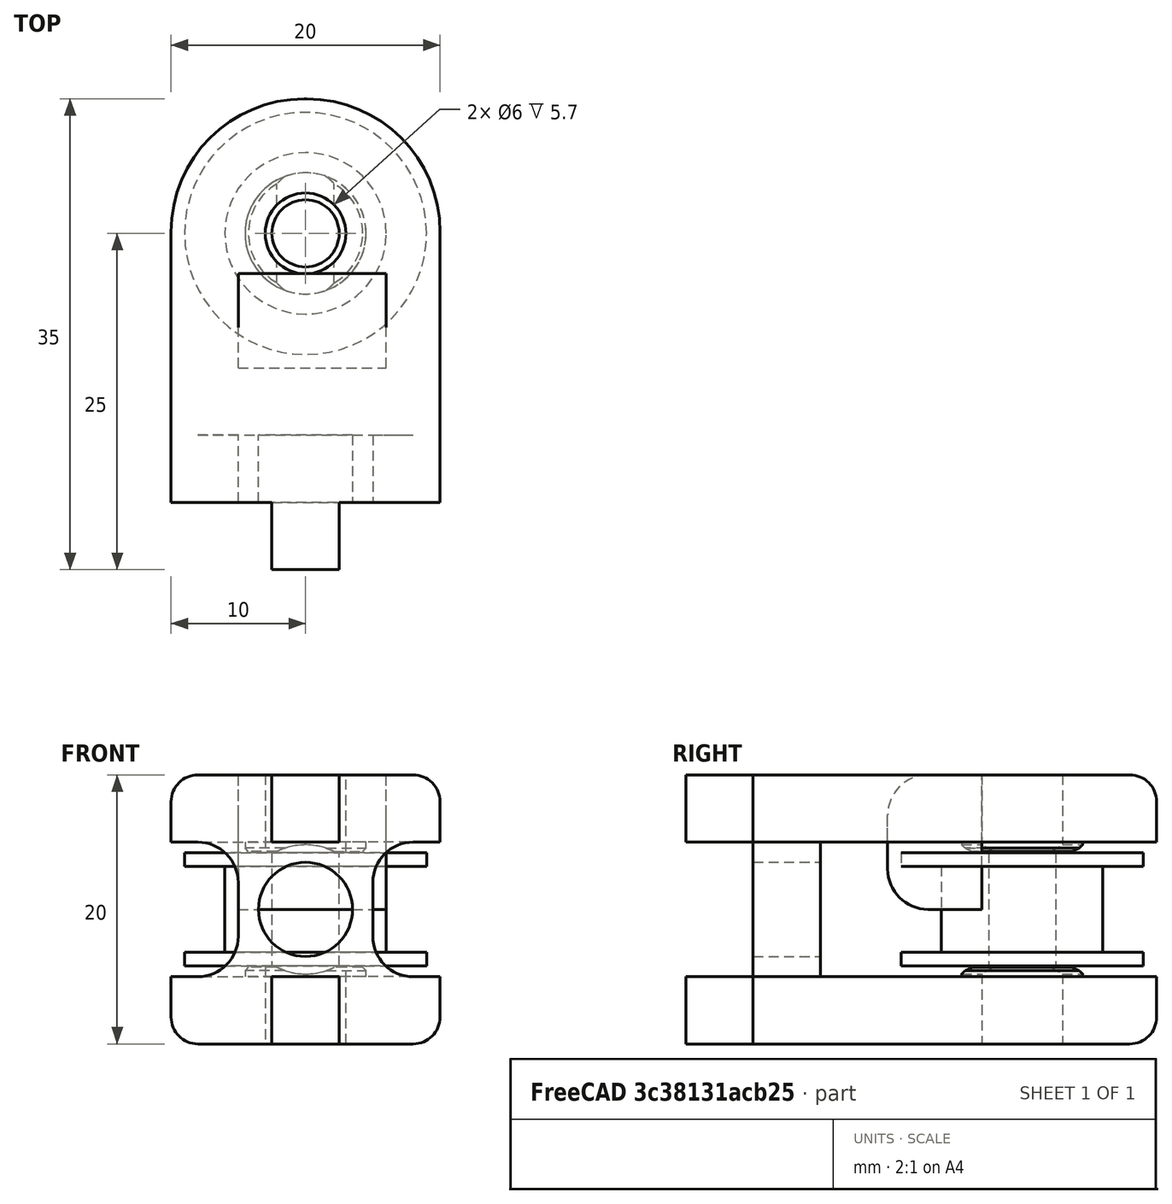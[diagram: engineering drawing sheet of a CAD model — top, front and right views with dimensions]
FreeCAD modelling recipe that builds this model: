
FCSTD DOCUMENT  (FreeCAD 0.20R29177 (Git))
Label: PoleaAcabados1
License: All rights reserved
LicenseURL: http://en.wikipedia.org/wiki/All_rights_reserved
objects: Part::Cylinder×7, Part::Cut×5, Part::Box×4, Part::FeaturePython×3, Part::MultiFuse×3, Part::Chamfer×3, Part::Refine×2, Part::Fillet×2, Part::Fuse×1, Spreadsheet::Sheet×1, PartDesign::FeatureBase×1, PartDesign::Fillet×1, PartDesign::Body×1
note: 33 computed .brp shape members not serialized (recipe doc carries the construction recipe); baked Part::Feature solids carry a one-line shape summary decoded from their .brp

FEATURE [Part::Cylinder] Cylinder002  label="Cilindro002"
  Angle = 360
  AttacherType = Attacher::AttachEngine3D
  FirstAngle = 0
  Height = 1
  Placement = pos=(0,0,-4.2) rot=(0,0,1;0rad)
  Radius = 9
  SecondAngle = 0
FEATURE [Part::Cylinder] Cylinder003  label="Cilindro003"
  Angle = 360
  AttacherType = Attacher::AttachEngine3D
  FirstAngle = 0
  Height = 10
  Placement = pos=(0,0,-5) rot=(0,0,1;0rad)
  Radius = 2.5
  SecondAngle = 0
FEATURE [Part::Fuse] Fusion001
  Base = -> Cylinder002
FEATURE [Part::Cut] Cut  label="Pulley"
  Base = -> Fusion001
  Placement = pos=(0,15,0) rot=(0,0,1;0rad)
  Tool = -> Cylinder003
  expr: .Placement.Base.y = Spreadsheet.viajPolea
FEATURE [Spreadsheet::Sheet] Spreadsheet
  cells = A1=Nombre; B1=Valor; A2=viajPolea; B2(viajPolea)=15; A3=tol; B3(tol)=1; A4=esp; B4(esp)=5; A5=prof; B5(prof)=20; A6=profMedio; B6(profMedio)==B5 / 2; A7=espDob; B7(espDob)==B4 * 2; A8=espMedio; B8(espMedio)==B4 / 2; A9=profMedREsp; B9(profMedREsp)==B6 - B4; A10=lonPol; B10(lonPol)==B2 + B6
FEATURE [Part::Box] Box  label="Base"
  AttacherType = Attacher::AttachEngine3D
  Height = 20
  Length = 20
  Placement = pos=(-10,-5,-10) rot=(0,0,1;0rad)
  Width = 5
  expr: .Placement.Base.x = -Spreadsheet.profMedio
  expr: .Placement.Base.y = -Spreadsheet.esp
  expr: .Placement.Base.z = -Spreadsheet.profMedio
  expr: Height = Spreadsheet.prof
  expr: Length = Spreadsheet.prof
  expr: Width = Spreadsheet.esp
FEATURE [Part::Box] Box001  label="pin0"
  AttacherType = Attacher::AttachEngine3D
  Height = 5
  Length = 5
  Placement = pos=(-2.5,-10,5) rot=(0,0,1;0rad)
  Width = 10
  expr: .Placement.Base.x = -Spreadsheet.espMedio
  expr: .Placement.Base.y = -Spreadsheet.espDob
  expr: .Placement.Base.z = Spreadsheet.profMedREsp
  expr: Height = Spreadsheet.esp
  expr: Length = Spreadsheet.esp
  expr: Width = Spreadsheet.espDob
FEATURE [Part::FeaturePython] Clone  label="pin001"  # Draft clone (typed FeaturePython)
  AttacherType = Attacher::AttachEngine3D
  Fuse = false
  Objects = -> [Box001]
  Placement = pos=(-2.5,-10,-10) rot=(0,0,1;0rad)
  Scale = (1,1,1)
  expr: .Placement.Base.y = -Spreadsheet.espDob
  expr: .Placement.Base.z = -Spreadsheet.profMedio
FEATURE [Part::Box] Box002  label="pared1"
  AttacherType = Attacher::AttachEngine3D
  Height = 5
  Length = 20
  Placement = pos=(-10,0,5) rot=(0,0,1;0rad)
  Width = 25
  expr: .Placement.Base.x = -Spreadsheet.profMedio
  expr: .Placement.Base.z = Spreadsheet.profMedREsp
  expr: Height = Spreadsheet.esp
  expr: Length = Spreadsheet.prof
  expr: Width = Spreadsheet.lonPol
FEATURE [Part::FeaturePython] Clone001  label="pared002"  # Draft clone (typed FeaturePython)
  AttacherType = Attacher::AttachEngine3D
  Fuse = false
  Objects = -> [Box002]
  Placement = pos=(-10,0,-10) rot=(0,0,1;0rad)
  Scale = (1,1,1)
  expr: .Placement.Base.z = -Spreadsheet.profMedio
FEATURE [Part::MultiFuse] Fusion
  Shapes = -> [Box,Box001,Clone,Box002,Clone001]
FEATURE [Part::Refine] Fusion002
  Source = -> Fusion
FEATURE [Part::Cylinder] Cylinder004  label="Cilindro004"
  Angle = 360
  AttacherType = Attacher::AttachEngine3D
  FirstAngle = 0
  Height = 30
  Placement = pos=(0,15,-15) rot=(0,0,1;0rad)
  Radius = 3
  SecondAngle = 0
  expr: .Placement.Base.y = Spreadsheet.viajPolea
FEATURE [Part::Box] Box007  label="Cubo005"
  AttacherType = Attacher::AttachEngine3D
  Height = 10
  Length = 11
  Placement = pos=(10,5,-5) rot=(0,0,1;0rad)
  Width = 7
FEATURE [PartDesign::FeatureBase] BaseFeature
  BaseFeature = -> Box007
FEATURE [PartDesign::Fillet] Fillet
  Base = -> BaseFeature [Edge10,Edge9]
  BaseFeature = -> BaseFeature
  Radius = 3
  SupportTransform = false
  UseAllEdges = false
FEATURE [PartDesign::Body] Body
  BaseFeature = -> Box007
  Group = -> [BaseFeature,Fillet]
  Origin = -> Origin
  Placement = pos=(-5,5,0) rot=(0,0,1;0rad)
  Tip = -> Fillet
FEATURE [Part::FeaturePython] Array  # Draft array (typed FeaturePython)
  AlwaysSyncPlacement = false
  Angle = 180
  ArrayType = 1
  Axis = (0,0,1)
  Base = -> Body
  Center = (0,0,0)
  Count = 2
  ExpandArray = false
  Fuse = false
  IntervalAxis = (0,0,0)
  IntervalX = (50,0,0)
  IntervalY = (0,50,0)
  IntervalZ = (0,0,50)
  NumberCircles = 3
  NumberPolar = 2
  NumberX = 2
  NumberY = 2
  NumberZ = 1
  Placement = pos=(0,-3,-5) rot=(0,0,1;1.5708rad)
  PlacementList = 2 placements: [(-5,5,0),(5,-5,0)]
  RadialDistance = 50
  ScaleList = (2) [(1,1,1),(1,1,1)]
  Symmetry = 1
  TangentialDistance = 25
  expr: .Placement.Base.z = -Spreadsheet.esp
FEATURE [Part::Cylinder] Cylinder  label="Cilindro"
  Angle = 360
  AttacherType = Attacher::AttachEngine3D
  FirstAngle = 0
  Height = 15
  Placement = pos=(0,5,0) rot=(1,0,0;1.5708rad)
  Radius = 3.5
  SecondAngle = 0
FEATURE [Part::Cylinder] Cylinder005  label="apoyo2"
  Angle = 360
  AttacherType = Attacher::AttachEngine3D
  FirstAngle = 0
  Height = 4
  Placement = pos=(0,0,-8.3) rot=(0,0,1;0rad)
  Radius = 4.5
  SecondAngle = 0
FEATURE [Part::Cylinder] Cylinder006  label="apoyo1"
  Angle = 360
  AttacherType = Attacher::AttachEngine3D
  FirstAngle = 0
  Height = 4
  Placement = pos=(0,0,4.3) rot=(0,0,1;0rad)
  Radius = 4.5
  SecondAngle = 0
FEATURE [Part::MultiFuse] Fusion003
  Placement = pos=(0,15,0) rot=(0,0,1;0rad)
  Shapes = -> [Cylinder005,Cylinder006]
  expr: .Placement.Base.y = Spreadsheet.viajPolea
FEATURE [Part::MultiFuse] Fusion004
  Shapes = -> [Fusion002,Fusion003]
FEATURE [Part::Refine] Fusion004001
  Source = -> Fusion004
FEATURE [Part::Cut] Cut001
  Base = -> Fusion004001
  Tool = -> Cylinder
FEATURE [Part::Cut] Cut002
  Base = -> Cut001
  Tool = -> Cylinder004
FEATURE [Part::Cut] Cut003
  Base = -> Cut002
  Tool = -> Array
FEATURE [Part::Cylinder] Cylinder007  label="Cilindro005"
  Angle = 360
  AttacherType = Attacher::AttachEngine3D
  FirstAngle = 0
  Height = 15
  Placement = pos=(0,23,0) rot=(1,0,0;1.5708rad)
  Radius = 4.8
  SecondAngle = 0
FEATURE [Part::Cut] Cut004
  Base = -> Cut003
  Tool = -> Cylinder007
FEATURE [Part::Chamfer] Chamfer
  Base = -> Cut004
  Edges = 2 edges r=0.25: [Edge123,Edge127]
FEATURE [Part::Chamfer] Chamfer001
  Base = -> Chamfer
  Edges = 1 edges r=0.25: [Edge4]
FEATURE [Part::Chamfer] Chamfer002
  Base = -> Chamfer001
  Edges = 3 edges r=0.25: [Edge125,Edge127,Edge129]
FEATURE [Part::Fillet] Fillet001
  Base = -> Chamfer002
  Edges = 4 edges r=9.9: [Edge33,Edge50,Edge107,Edge120]
FEATURE [Part::Fillet] Fillet002
  Base = -> Fillet001
  Edges = 2 edges r=2: [Edge12,Edge115]
